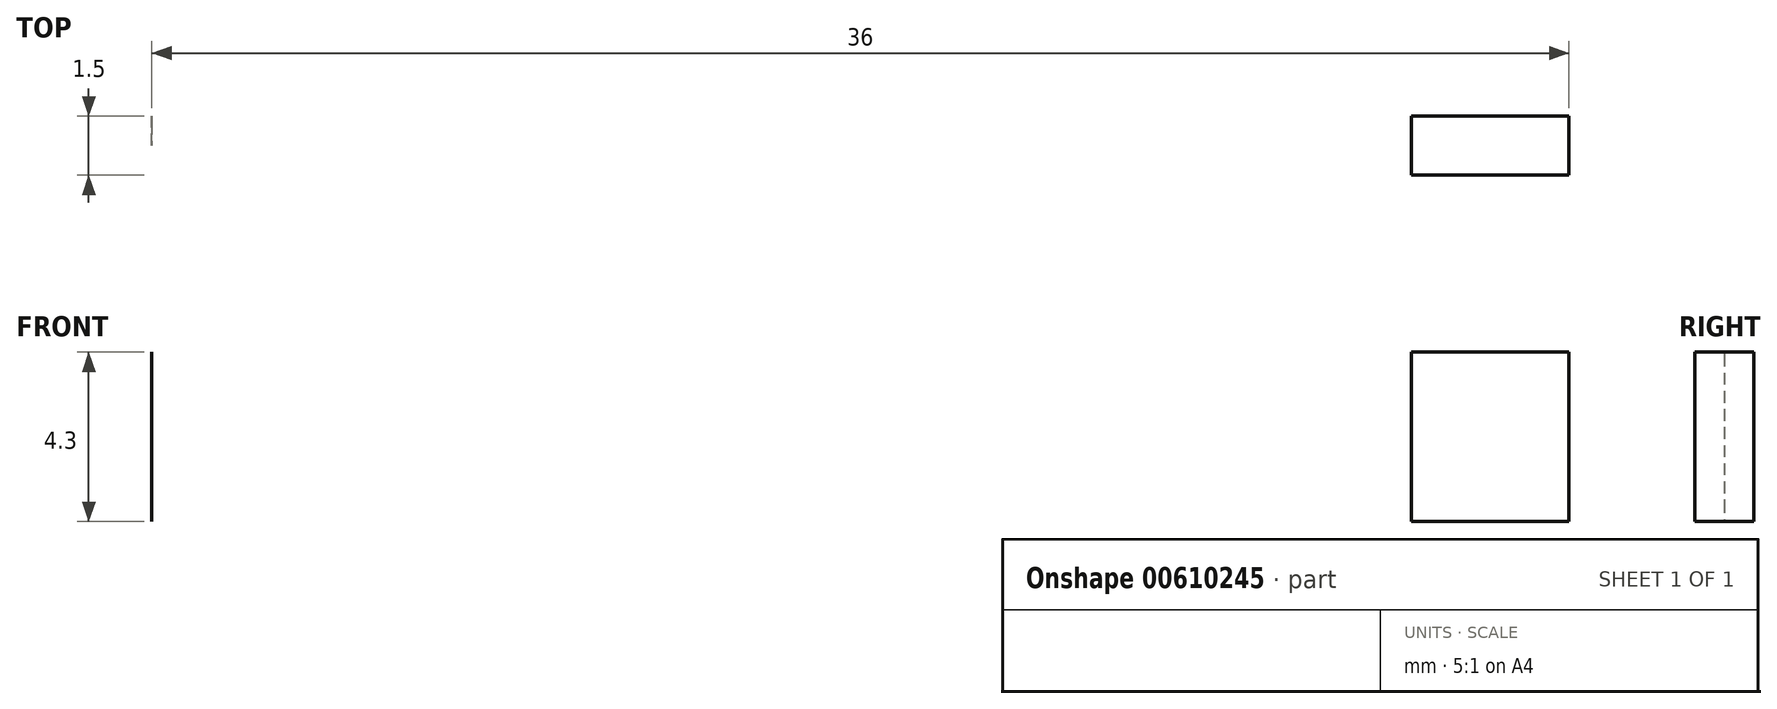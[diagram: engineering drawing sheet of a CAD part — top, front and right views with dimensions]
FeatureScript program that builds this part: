
annotation { "Feature Type Name" : "Feature", "Feature Type Description" : "" }
export const myFeature = defineFeature(function(context is Context, id is Id, definition is map)
    precondition{}
    {
        {
            var Q0;
            Q0=qCreatedBy(makeId("Right.planeOp"),FACE);
            var sketch = newSketch(context, id + "F0", { "sketchPlane" : qUnion([Q0])});
            skLineSegment(sketch, "E0.0", {"start": v(-55.17, 9.5) * mm, "end": v(-40.57, 9.5) * mm});
            skLineSegment(sketch, "E1", {"start": v(-56.17, 8.5) * mm, "end": v(-56.17, 1) * mm});
            skLineSegment(sketch, "E2", {"start": v(-36.37, 9.5) * mm, "end": v(-36.37, 8.5) * mm});
            skLineSegment(sketch, "E3", {"start": v(-40.57, 9.5) * mm, "end": v(-40.57, 8.5) * mm});
            skArc(sketch, "E4", {"start": v(-40.57, 8.5) * mm, "mid": v(-38.47, 6.34) * mm, "end": v(-36.37, 8.5) * mm});
            skLineSegment(sketch, "E5.1.0.0", {"start": v(-35.07, 9.5) * mm, "end": v(-35.07, 8.5) * mm});
            skArc(sketch, "E5.1.0.1", {"start": v(-35.07, 8.5) * mm, "mid": v(-32.97, 6.34) * mm, "end": v(-30.87, 8.5) * mm});
            skLineSegment(sketch, "E5.1.0.2", {"start": v(-30.87, 9.5) * mm, "end": v(-30.87, 8.5) * mm});
            skLineSegment(sketch, "E5.2.0.0", {"start": v(-29.57, 9.5) * mm, "end": v(-29.57, 8.5) * mm});
            skArc(sketch, "E5.2.0.1", {"start": v(-29.57, 8.5) * mm, "mid": v(-27.47, 6.34) * mm, "end": v(-25.37, 8.5) * mm});
            skLineSegment(sketch, "E5.2.0.2", {"start": v(-25.37, 9.5) * mm, "end": v(-25.37, 8.5) * mm});
            skLineSegment(sketch, "E5.3.0.0", {"start": v(-24.07, 9.5) * mm, "end": v(-24.07, 8.5) * mm});
            skArc(sketch, "E5.3.0.1", {"start": v(-24.07, 8.5) * mm, "mid": v(-21.97, 6.34) * mm, "end": v(-19.87, 8.5) * mm});
            skLineSegment(sketch, "E5.3.0.2", {"start": v(-19.87, 9.5) * mm, "end": v(-19.87, 8.5) * mm});
            skLineSegment(sketch, "E5.4.0.0", {"start": v(-18.57, 9.5) * mm, "end": v(-18.57, 8.5) * mm});
            skArc(sketch, "E5.4.0.1", {"start": v(-18.57, 8.5) * mm, "mid": v(-16.47, 6.34) * mm, "end": v(-14.37, 8.5) * mm});
            skLineSegment(sketch, "E5.4.0.2", {"start": v(-14.37, 9.5) * mm, "end": v(-14.37, 8.5) * mm});
            skLineSegment(sketch, "E5.5.0.0", {"start": v(-13.07, 9.5) * mm, "end": v(-13.07, 8.5) * mm});
            skArc(sketch, "E5.5.0.1", {"start": v(-13.07, 8.5) * mm, "mid": v(-10.97, 6.34) * mm, "end": v(-8.87, 8.5) * mm});
            skLineSegment(sketch, "E5.5.0.2", {"start": v(-8.87, 9.5) * mm, "end": v(-8.87, 8.5) * mm});
            skLineSegment(sketch, "E5.6.0.0", {"start": v(-7.57, 9.5) * mm, "end": v(-7.57, 8.5) * mm});
            skArc(sketch, "E5.6.0.1", {"start": v(-7.57, 8.5) * mm, "mid": v(-5.47, 6.34) * mm, "end": v(-3.37, 8.5) * mm});
            skLineSegment(sketch, "E5.6.0.2", {"start": v(-3.37, 9.5) * mm, "end": v(-3.37, 8.5) * mm});
            skLineSegment(sketch, "E5.7.0.0", {"start": v(-2.07, 9.5) * mm, "end": v(-2.07, 8.5) * mm});
            skArc(sketch, "E5.7.0.1", {"start": v(-2.07, 8.5) * mm, "mid": v(0.03, 6.34) * mm, "end": v(2.13, 8.5) * mm});
            skLineSegment(sketch, "E5.7.0.2", {"start": v(2.13, 9.5) * mm, "end": v(2.13, 8.5) * mm});
            skLineSegment(sketch, "E5.8.0.0", {"start": v(3.43, 9.5) * mm, "end": v(3.43, 8.5) * mm});
            skArc(sketch, "E5.8.0.1", {"start": v(3.43, 8.5) * mm, "mid": v(5.53, 6.34) * mm, "end": v(7.63, 8.5) * mm});
            skLineSegment(sketch, "E5.8.0.2", {"start": v(7.63, 9.5) * mm, "end": v(7.63, 8.5) * mm});
            skLineSegment(sketch, "E5.9.0.0", {"start": v(8.93, 9.5) * mm, "end": v(8.93, 8.5) * mm});
            skArc(sketch, "E5.9.0.1", {"start": v(8.93, 8.5) * mm, "mid": v(11.03, 6.34) * mm, "end": v(13.13, 8.5) * mm});
            skLineSegment(sketch, "E5.9.0.2", {"start": v(13.13, 9.5) * mm, "end": v(13.13, 8.5) * mm});
            skLineSegment(sketch, "E5.10.0.0", {"start": v(14.43, 9.5) * mm, "end": v(14.43, 8.5) * mm});
            skArc(sketch, "E5.10.0.1", {"start": v(14.43, 8.5) * mm, "mid": v(16.53, 6.34) * mm, "end": v(18.63, 8.5) * mm});
            skLineSegment(sketch, "E5.10.0.2", {"start": v(18.63, 9.5) * mm, "end": v(18.63, 8.5) * mm});
            skLineSegment(sketch, "E5.11.0.0", {"start": v(19.93, 9.5) * mm, "end": v(19.93, 8.5) * mm});
            skArc(sketch, "E5.11.0.1", {"start": v(19.93, 8.5) * mm, "mid": v(22.03, 6.34) * mm, "end": v(24.13, 8.5) * mm});
            skLineSegment(sketch, "E5.11.0.2", {"start": v(24.13, 9.5) * mm, "end": v(24.13, 8.5) * mm});
            skLineSegment(sketch, "E5.direction1", {"start": v(-40.57, 8.5) * mm, "end": v(-35.07, 8.5) * mm, "construction": true});
            skLineSegment(sketch, "E6.0.12.0", {"start": v(25.43, 9.5) * mm, "end": v(25.43, 8.5) * mm});
            skArc(sketch, "E6.3.12.0", {"start": v(25.43, 8.5) * mm, "mid": v(27.53, 6.34) * mm, "end": v(29.63, 8.5) * mm});
            skLineSegment(sketch, "E6.7.12.0", {"start": v(29.63, 9.5) * mm, "end": v(29.63, 8.5) * mm});
            skLineSegment(sketch, "E6.0.13.0", {"start": v(30.93, 9.5) * mm, "end": v(30.93, 8.5) * mm});
            skArc(sketch, "E6.3.13.0", {"start": v(30.93, 8.5) * mm, "mid": v(33.03, 6.34) * mm, "end": v(35.13, 8.5) * mm});
            skLineSegment(sketch, "E6.7.13.0", {"start": v(35.13, 9.5) * mm, "end": v(35.13, 8.5) * mm});
            skLineSegment(sketch, "E6.0.14.0", {"start": v(36.43, 9.5) * mm, "end": v(36.43, 8.5) * mm});
            skArc(sketch, "E6.3.14.0", {"start": v(36.43, 8.5) * mm, "mid": v(38.46, 6.34) * mm, "end": v(40.63, 8.36) * mm});
            skLineSegment(sketch, "E6.7.14.0", {"start": v(40.63, 9.5) * mm, "end": v(40.63, 8.5) * mm});
            skLineSegment(sketch, "E7", {"start": v(40.63, 8.5) * mm, "end": v(40.63, 8.36) * mm});
            skLineSegment(sketch, "E8.0", {"start": v(41.83, 9.1) * mm, "end": v(41.83, 5.49) * mm});
            skPoint(sketch, "E9.visualSharp", {"position": v(41.83, 9.5) * mm});
            skArc(sketch, "E9.filletArc", {"start": v(41.83, 9.1) * mm, "mid": v(41.71, 9.38) * mm, "end": v(41.43, 9.5) * mm});
            skPoint(sketch, "E10.visualSharp", {"position": v(41.83, 4.49) * mm});
            skArc(sketch, "E10.filletArc", {"start": v(41.83, 5.49) * mm, "mid": v(42.12, 4.78) * mm, "end": v(42.83, 4.49) * mm});
            skPoint(sketch, "E11.visualSharp", {"position": v(-56.17, 9.5) * mm});
            skArc(sketch, "E11.filletArc", {"start": v(-55.17, 9.5) * mm, "mid": v(-55.87, 9.2) * mm, "end": v(-56.17, 8.5) * mm});
            skPoint(sketch, "E12.visualSharp", {"position": v(-56.17, 0) * mm});
            skArc(sketch, "E12.filletArc", {"start": v(-56.17, 1) * mm, "mid": v(-55.87, 0.3) * mm, "end": v(-55.17, 0) * mm});
            skLineSegment(sketch, "E13.trimOffspring", {"start": v(-36.37, 9.5) * mm, "end": v(-35.07, 9.5) * mm});
            skLineSegment(sketch, "E14.trimOffspring", {"start": v(-30.87, 9.5) * mm, "end": v(-29.57, 9.5) * mm});
            skLineSegment(sketch, "E15.trimOffspring", {"start": v(-25.37, 9.5) * mm, "end": v(-24.07, 9.5) * mm});
            skLineSegment(sketch, "E16.trimOffspring", {"start": v(-19.87, 9.5) * mm, "end": v(-18.57, 9.5) * mm});
            skLineSegment(sketch, "E17.trimOffspring", {"start": v(-14.37, 9.5) * mm, "end": v(-13.07, 9.5) * mm});
            skLineSegment(sketch, "E18.trimOffspring", {"start": v(-8.87, 9.5) * mm, "end": v(-7.57, 9.5) * mm});
            skLineSegment(sketch, "E19.trimOffspring", {"start": v(-3.37, 9.5) * mm, "end": v(-2.07, 9.5) * mm});
            skLineSegment(sketch, "E20.trimOffspring", {"start": v(2.13, 9.5) * mm, "end": v(3.43, 9.5) * mm});
            skLineSegment(sketch, "E21.trimOffspring", {"start": v(7.63, 9.5) * mm, "end": v(8.93, 9.5) * mm});
            skLineSegment(sketch, "E22.trimOffspring", {"start": v(13.13, 9.5) * mm, "end": v(14.43, 9.5) * mm});
            skLineSegment(sketch, "E23.trimOffspring", {"start": v(18.63, 9.5) * mm, "end": v(19.93, 9.5) * mm});
            skLineSegment(sketch, "E24.trimOffspring", {"start": v(24.13, 9.5) * mm, "end": v(25.43, 9.5) * mm});
            skLineSegment(sketch, "E25.trimOffspring", {"start": v(29.63, 9.5) * mm, "end": v(30.93, 9.5) * mm});
            skLineSegment(sketch, "E26.trimOffspring", {"start": v(35.13, 9.5) * mm, "end": v(36.43, 9.5) * mm});
            skLineSegment(sketch, "E27.trimOffspring", {"start": v(40.63, 9.5) * mm, "end": v(41.43, 9.5) * mm});
            skCircle(sketch, "E28", {"center": v(101.47, 6.6) * mm, "radius": 2.37 * mm});
            skFitSpline(sketch, "E29", {"points": [v(100.05, 0) * mm, v(101.63, 0.64) * mm, v(102.57, 1.67) * mm, v(103.16, 3.05) * mm, v(103.77, 6.06) * mm, v(103.77, 6.07) * mm], "startDerivative": vector(8.87, 1.77) * mm, "endDerivative": vector(0.05, 0.15) * mm});
            skFitSpline(sketch, "E30", {"points": [v(96.02, 4.49) * mm, v(98.08, 6) * mm, v(99.86, 8.33) * mm], "startDerivative": vector(7.69, 2.2) * mm, "endDerivative": vector(4.53, 3.82) * mm});
            skLineSegment(sketch, "E31", {"start": v(-55.17, 0) * mm, "end": v(100.05, 0) * mm});
            skLineSegment(sketch, "E32", {"start": v(96.02, 4.49) * mm, "end": v(42.83, 4.49) * mm});
            skSolve(sketch);
        }
        {
            var Q0;
            Q0=makeQuery(id+"F0.imprint","IMPRINT",FACE,{"disambiguationData":[TD([[makeQuery(id+"F0.imprint","IMPRINT",EDGE,{"derivedFrom":sQuery(id+"F0.wireOp",EDGE,"E0.0")}),-1.0]])]});
            extrude(context, id + "F1", {"entities" : qUnion([Q0]), "endBound" : BoundingType.SYMMETRIC, "depth" : 32 * mm, "offsetDistance" : 25 * mm});
        }
        {
            var Q0;
            Q0=qCreatedBy(makeId("Right.planeOp"),FACE);
            var sketch = newSketch(context, id + "F2", { "sketchPlane" : qUnion([Q0])});
            skCircle(sketch, "E33", {"center": v(101.47, 6.6) * mm, "radius": 2.36 * mm});
            skPoint(sketch, "E33.first.point", {"position": v(103.61, 5.6) * mm});
            skPoint(sketch, "E33.second.point", {"position": v(100.13, 4.65) * mm});
            skPoint(sketch, "E33.third.point", {"position": v(99.48, 7.88) * mm});
            skSolve(sketch);
        }
        {
            var Q0;
            Q0=makeQuery(id+"F2.imprint","IMPRINT",FACE,{"disambiguationData":[TD([[makeQuery(id+"F2.imprint","IMPRINT",EDGE,{"derivedFrom":sQuery(id+"F2.wireOp",EDGE,"E33")}),1.0]])]});
            extrude(context, id + "F3", {"entities" : qUnion([Q0]), "operationType" : NewBodyOperationType.ADD, "endBound" : BoundingType.SYMMETRIC, "depth" : 40 * mm, "offsetDistance" : 25 * mm});
        }
        {
            var Q0;
            Q0=qCreatedBy(makeId("Top.planeOp"),FACE);
            var sketch = newSketch(context, id + "F4", { "sketchPlane" : qUnion([Q0])});
            skLineSegment(sketch, "E34.0", {"start": v(-4.68, 104.08) * mm, "end": v(-4.68, 69.65) * mm});
            skLineSegment(sketch, "E35.0", {"start": v(4.68, 104.08) * mm, "end": v(4.68, 69.65) * mm});
            skLineSegment(sketch, "E36", {"start": v(-4.68, 69.65) * mm, "end": v(4.68, 69.65) * mm});
            skLineSegment(sketch, "E37", {"start": v(4.68, 104.08) * mm, "end": v(-4.68, 104.08) * mm});
            skSolve(sketch);
        }
        {
            var Q0;
            Q0 = qSketchRegion(id + "F4", true);
            extrude(context, id + "F5", {"entities" : qUnion([Q0]), "operationType" : NewBodyOperationType.REMOVE, "endBound" : BoundingType.SYMMETRIC, "oppositeDirection" : true, "depth" : -25 * mm, "offsetDistance" : 25 * mm});
        }
        {
            var Q0;
            Q0=qCreatedBy(makeId("Top.planeOp"),FACE);
            var sketch = newSketch(context, id + "F6", { "sketchPlane" : qUnion([Q0])});
            skLineSegment(sketch, "E38.0", {"start": v(-16, 102.2) * mm, "end": v(-16, 102.2) * mm});
            skLineSegment(sketch, "E39.0", {"start": v(-16, 100.7) * mm, "end": v(-16, 100.7) * mm});
            skLineSegment(sketch, "E40", {"start": v(-16, 102.2) * mm, "end": v(-16, 100.7) * mm});
            skPoint(sketch, "E41.startSnap0", {"position": v(-16, 101.45) * mm});
            skLineSegment(sketch, "E42.0", {"start": v(-20, 100.7) * mm, "end": v(-16, 100.7) * mm});
            skLineSegment(sketch, "E43.0", {"start": v(-20, 102.2) * mm, "end": v(-16, 102.2) * mm});
            skLineSegment(sketch, "E44", {"start": v(16, 101.45) * mm, "end": v(16, 102.2) * mm});
            skLineSegment(sketch, "E45", {"start": v(16, 101.45) * mm, "end": v(16, 100.7) * mm});
            skLineSegment(sketch, "E46.trimOffspring", {"start": v(16, 102.2) * mm, "end": v(20, 102.2) * mm});
            skLineSegment(sketch, "E47.trimOffspring", {"start": v(16, 100.7) * mm, "end": v(20, 100.7) * mm});
            skLineSegment(sketch, "E48", {"start": v(-20, 102.2) * mm, "end": v(-20, 100.7) * mm});
            skLineSegment(sketch, "E49", {"start": v(20, 100.7) * mm, "end": v(20, 102.2) * mm});
            skSolve(sketch);
        }
        {
            var Q0;
            Q0=makeQuery(id+"F6.imprint","IMPRINT",FACE,{"disambiguationData":[TD([[makeQuery(id+"F6.imprint","IMPRINT",EDGE,{"derivedFrom":sQuery(id+"F6.wireOp",EDGE,"E44")}),-1.0]])]});
            var Q1;
            Q1=makeQuery(id+"F6.imprint","IMPRINT",FACE,{"disambiguationData":[TD([[makeQuery(id+"F6.imprint","IMPRINT",EDGE,{"derivedFrom":sQuery(id+"F6.wireOp",EDGE,"E40")}),-1.0]])]});
            extrude(context, id + "F7", {"entities" : qUnion([Q0, Q1]), "operationType" : NewBodyOperationType.ADD, "depth" : 4.3 * mm, "offsetDistance" : 25 * mm});
        }
    });
